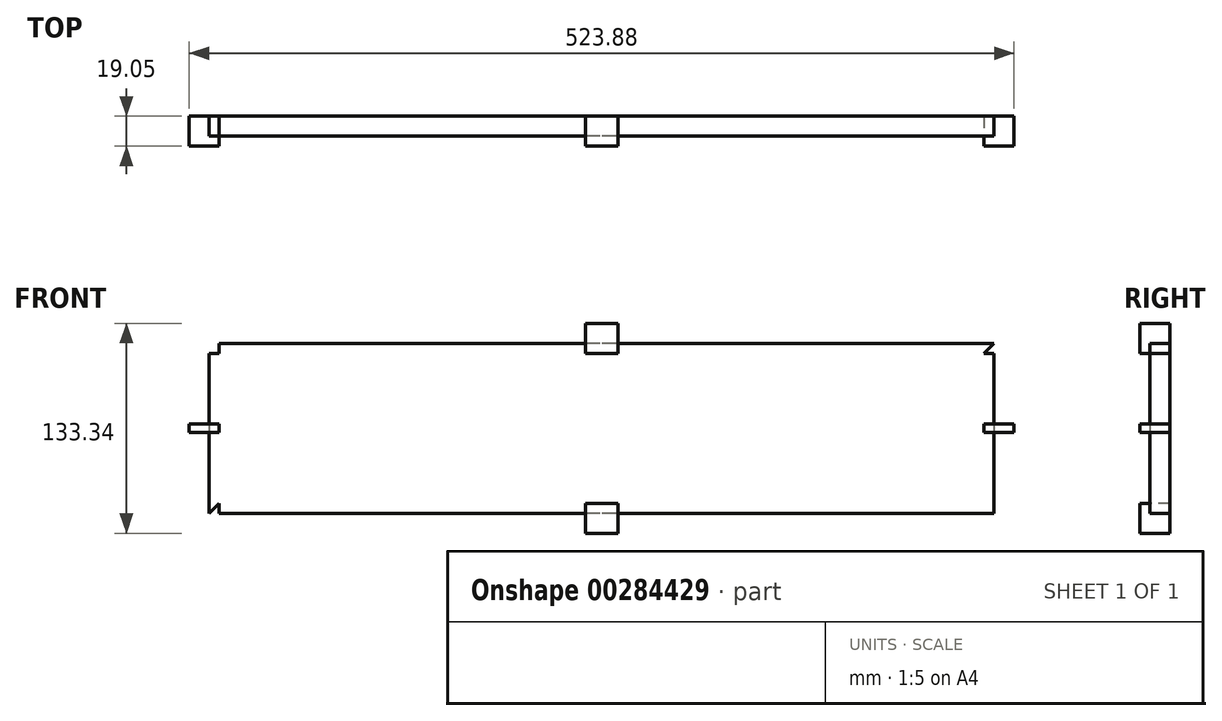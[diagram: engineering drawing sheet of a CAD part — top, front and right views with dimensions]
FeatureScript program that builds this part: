
annotation { "Feature Type Name" : "Feature", "Feature Type Description" : "" }
export const myFeature = defineFeature(function(context is Context, id is Id, definition is map)
    precondition{}
    {
        {
            assignVariable(context, id + "F0", {"name" : "Width", "anyValue" : 20.62});
        }
        {
            assignVariable(context, id + "F1", {"name" : "Height", "anyValue" : 5.25});
        }
        {
            var Q0;
            Q0=qCreatedBy(makeId("Front.planeOp"),FACE);
            var sketch = newSketch(context, id + "F2", { "sketchPlane" : qUnion([Q0])});
            skLineSegment(sketch, "E0.bottom", {"start": v(249.24, 53.98) * mm, "end": v(-249.24, 53.98) * mm});
            skLineSegment(sketch, "E0.top", {"start": v(249.24, -53.98) * mm, "end": v(-249.24, -53.98) * mm});
            skLineSegment(sketch, "E0.left", {"start": v(249.24, 53.98) * mm, "end": v(249.24, -53.98) * mm});
            skLineSegment(sketch, "E0.right", {"start": v(-249.24, 53.98) * mm, "end": v(-249.24, -53.98) * mm});
            skPoint(sketch, "E0.middle", {"position": v(0, 0) * mm});
            skSolve(sketch);
        }
        {
            var Q0;
            Q0=makeQuery(id+"F2.imprint","IMPRINT",FACE,{"disambiguationData":[TD([[makeQuery(id+"F2.imprint","IMPRINT",EDGE,{"derivedFrom":sQuery(id+"F2.wireOp",EDGE,"E0.bottom")}),1.0]])]});
            extrude(context, id + "F3", {"entities" : qUnion([Q0]), "depth" : 12.7 * mm});
        }
        {
            var Q0;
            Q0=qCreatedBy(makeId("Top.planeOp"),FACE);
            var sketch = newSketch(context, id + "F4", { "sketchPlane" : qUnion([Q0])});
            skLineSegment(sketch, "E1", {"start": v(-261.94, 0) * mm, "end": v(-261.94, -19.05) * mm});
            skLineSegment(sketch, "E2", {"start": v(-261.94, -19.05) * mm, "end": v(-242.89, -19.05) * mm});
            skLineSegment(sketch, "E3", {"start": v(-242.89, -19.05) * mm, "end": v(-242.89, -12.7) * mm});
            skLineSegment(sketch, "E4", {"start": v(-242.89, -12.7) * mm, "end": v(-249.24, -12.7) * mm});
            skLineSegment(sketch, "E5", {"start": v(-249.24, -12.7) * mm, "end": v(-249.24, 0) * mm});
            skLineSegment(sketch, "E6", {"start": v(-249.24, 0) * mm, "end": v(-261.94, 0) * mm});
            skSolve(sketch);
        }
        {
            var Q0;
            Q0=makeQuery(id+"F4.imprint","IMPRINT",FACE,{"disambiguationData":[TD([[makeQuery(id+"F4.imprint","IMPRINT",EDGE,{"derivedFrom":sQuery(id+"F4.wireOp",EDGE,"E1")}),1.0]])]});
            extrude(context, id + "F5", {"entities" : qUnion([Q0]), "depth" : (getVariable(context, 'Height') / 2) * mm, "hasSecondDirection" : true, "secondDirectionOppositeDirection" : true, "secondDirectionDepth" : (getVariable(context, 'Height') / 2) * mm});
        }
        {
            var Q0;
            Q0=makeQuery(id+"F5.opExtrude","SWEPT_FACE",FACE,{"disambiguationData":[OSD([sQuery(id+"F4.wireOp",EDGE,"E2")])]});
            var sketch = newSketch(context, id + "F6", { "sketchPlane" : qUnion([Q0])});
            skLineSegment(sketch, "E7", {"start": v(-261.94, 66.68) * mm, "end": v(-242.89, 47.63) * mm});
            skLineSegment(sketch, "E8", {"start": v(-242.89, 47.63) * mm, "end": v(-242.89, 66.68) * mm});
            skLineSegment(sketch, "E9", {"start": v(-242.89, 66.68) * mm, "end": v(-261.94, 66.68) * mm});
            skLineSegment(sketch, "E10.MirrorCS", {"start": v(-261.94, -66.68) * mm, "end": v(-242.89, -47.63) * mm});
            skLineSegment(sketch, "E11.MirrorCS", {"start": v(-242.89, -47.63) * mm, "end": v(-242.89, -66.68) * mm});
            skLineSegment(sketch, "E12.MirrorCS", {"start": v(-242.89, -66.68) * mm, "end": v(-261.94, -66.68) * mm});
            skSolve(sketch);
        }
        {
            var Q0;
            Q0 = qSketchRegion(id + "F6", true);
            extrude(context, id + "F7", {"entities" : qUnion([Q0]), "operationType" : NewBodyOperationType.REMOVE, "endBound" : BoundingType.THROUGH_ALL, "oppositeDirection" : true, "depth" : 25.4 * mm});
        }
        {
            var Q0;
            Q0=qCreatedBy(makeId("Right.planeOp"),FACE);
            var sketch = newSketch(context, id + "F8", { "sketchPlane" : qUnion([Q0])});
            skLineSegment(sketch, "E13", {"start": v(0, 66.68) * mm, "end": v(-19.05, 66.68) * mm});
            skLineSegment(sketch, "E14", {"start": v(-19.05, 66.68) * mm, "end": v(-19.05, 47.63) * mm});
            skLineSegment(sketch, "E15", {"start": v(-19.05, 47.63) * mm, "end": v(-12.7, 47.63) * mm});
            skLineSegment(sketch, "E16", {"start": v(-12.7, 47.63) * mm, "end": v(-12.7, 53.98) * mm});
            skLineSegment(sketch, "E17", {"start": v(-12.7, 53.98) * mm, "end": v(0, 53.98) * mm});
            skLineSegment(sketch, "E18", {"start": v(0, 53.98) * mm, "end": v(0, 66.68) * mm});
            skSolve(sketch);
        }
        {
            var Q0;
            Q0 = qSketchRegion(id + "F8", true);
            extrude(context, id + "F9", {"entities" : qUnion([Q0]), "depth" : (getVariable(context, 'Width') / 2) * mm, "hasSecondDirection" : true, "secondDirectionOppositeDirection" : true, "secondDirectionDepth" : (getVariable(context, 'Width') / 2) * mm});
        }
        {
            var Q0;
            Q0=makeQuery(id+"F9.opExtrude","SWEPT_FACE",FACE,{"disambiguationData":[OSD([sQuery(id+"F8.wireOp",EDGE,"E14")])]});
            var sketch = newSketch(context, id + "F10", { "sketchPlane" : qUnion([Q0])});
            skLineSegment(sketch, "E19", {"start": v(-261.94, 66.68) * mm, "end": v(-242.89, 47.63) * mm});
            skLineSegment(sketch, "E20", {"start": v(-242.89, 47.63) * mm, "end": v(-261.94, 47.63) * mm});
            skLineSegment(sketch, "E21", {"start": v(-261.94, 47.63) * mm, "end": v(-261.94, 66.68) * mm});
            skLineSegment(sketch, "E22.MirrorCS", {"start": v(242.89, 47.63) * mm, "end": v(261.94, 47.63) * mm});
            skLineSegment(sketch, "E23.MirrorCS", {"start": v(261.94, 47.63) * mm, "end": v(261.94, 66.68) * mm});
            skLineSegment(sketch, "E24.MirrorCS", {"start": v(261.94, 66.68) * mm, "end": v(242.89, 47.63) * mm});
            skSolve(sketch);
        }
        {
            var Q0;
            Q0 = qSketchRegion(id + "F10", true);
            extrude(context, id + "F11", {"entities" : qUnion([Q0]), "operationType" : NewBodyOperationType.REMOVE, "endBound" : BoundingType.THROUGH_ALL, "oppositeDirection" : true, "depth" : 25.4 * mm});
        }
        {
            var Q0;
            Q0=makeQuery(id+"F5.opExtrude","SWEPT_BODY",BODY,{"disambiguationData":[OSD([sQuery(id+"F4.wireOp",EDGE,"E1"),sQuery(id+"F4.wireOp",EDGE,"E2"),sQuery(id+"F4.wireOp",EDGE,"E3"),sQuery(id+"F4.wireOp",EDGE,"E4"),sQuery(id+"F4.wireOp",EDGE,"E5"),sQuery(id+"F4.wireOp",EDGE,"E6")])]});
            var Q1;
            Q1=qCreatedBy(makeId("Right.planeOp"),FACE);
            mirror(context, id + "F12", {"entities" : qUnion([Q0]), "mirrorPlane" : qUnion([Q1])});
        }
        {
            var Q0;
            Q0=makeQuery(id+"F9.opExtrude","SWEPT_BODY",BODY,{"disambiguationData":[OSD([sQuery(id+"F8.wireOp",EDGE,"E13"),sQuery(id+"F8.wireOp",EDGE,"E14"),sQuery(id+"F8.wireOp",EDGE,"E15"),sQuery(id+"F8.wireOp",EDGE,"E16"),sQuery(id+"F8.wireOp",EDGE,"E17"),sQuery(id+"F8.wireOp",EDGE,"E18")])]});
            var Q1;
            Q1=qCreatedBy(makeId("Top.planeOp"),FACE);
            mirror(context, id + "F13", {"entities" : qUnion([Q0]), "mirrorPlane" : qUnion([Q1])});
        }
    });
